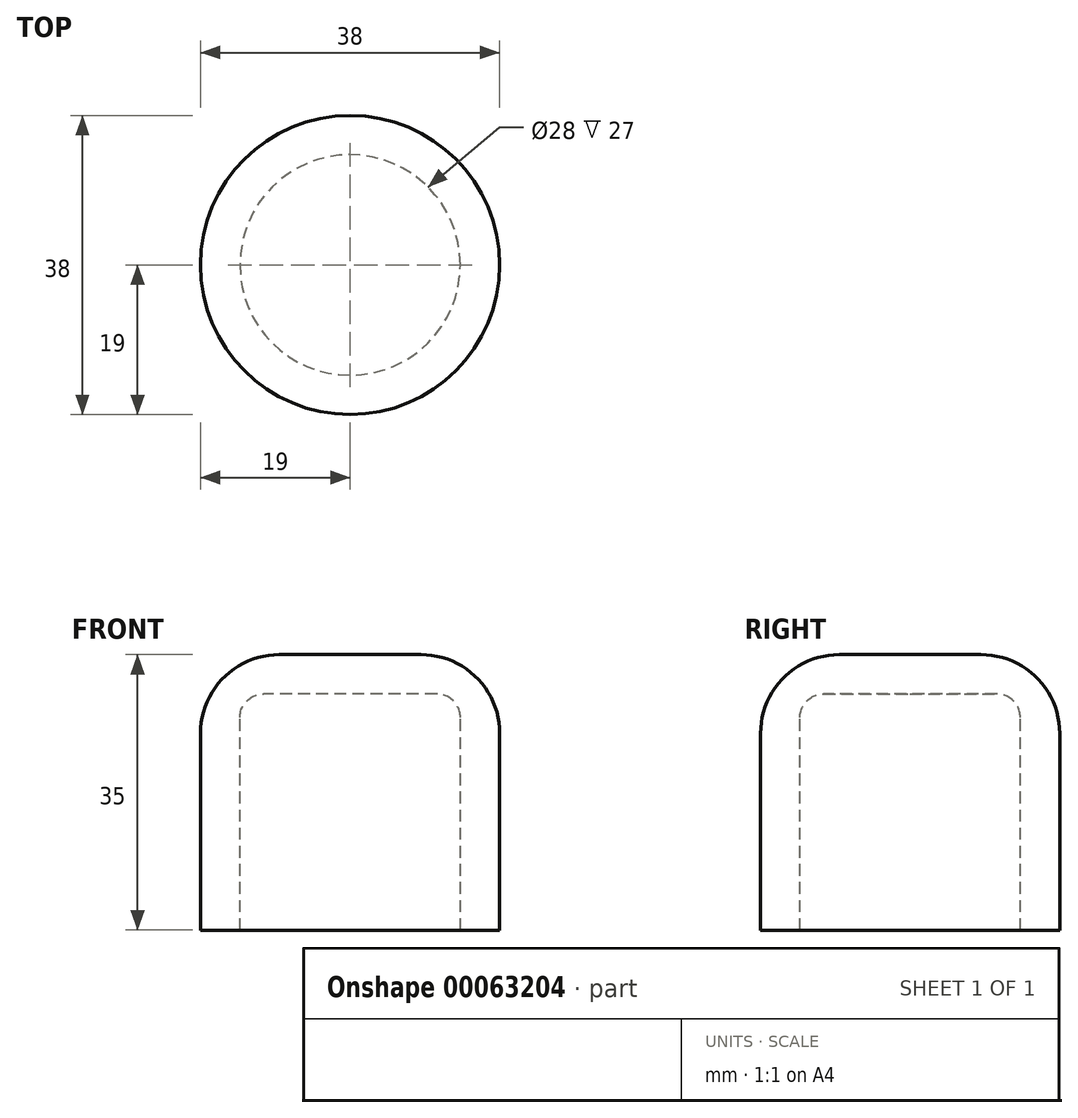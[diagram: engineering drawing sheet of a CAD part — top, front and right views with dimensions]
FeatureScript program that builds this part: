
annotation { "Feature Type Name" : "Feature", "Feature Type Description" : "" }
export const myFeature = defineFeature(function(context is Context, id is Id, definition is map)
    precondition{}
    {
        {
            var Q0;
            Q0=qCreatedBy(makeId("Front.planeOp"),FACE);
            var sketch = newSketch(context, id + "F0", { "sketchPlane" : qUnion([Q0])});
            skLineSegment(sketch, "E0", {"start": v(-14, -1.38) * mm, "end": v(-14, 25.62) * mm});
            skLineSegment(sketch, "E1", {"start": v(-11, 28.62) * mm, "end": v(0, 28.62) * mm});
            skLineSegment(sketch, "E2", {"start": v(0, 28.62) * mm, "end": v(0, -1.46) * mm});
            skLineSegment(sketch, "E3.0", {"start": v(-9, 33.62) * mm, "end": v(0, 33.62) * mm});
            skLineSegment(sketch, "E3.1", {"start": v(-19, -1.38) * mm, "end": v(-19, 23.62) * mm});
            skLineSegment(sketch, "E4", {"start": v(0, 28.62) * mm, "end": v(0, 33.62) * mm});
            skLineSegment(sketch, "E5", {"start": v(-14, -1.38) * mm, "end": v(-19, -1.38) * mm});
            skPoint(sketch, "E6.visualSharp", {"position": v(-14, 28.62) * mm});
            skArc(sketch, "E6.filletArc", {"start": v(-11, 28.62) * mm, "mid": v(-13.12, 27.74) * mm, "end": v(-14, 25.62) * mm});
            skPoint(sketch, "E7.visualSharp", {"position": v(-19, 33.62) * mm});
            skArc(sketch, "E7.filletArc", {"start": v(-9, 33.62) * mm, "mid": v(-16.07, 30.7) * mm, "end": v(-19, 23.62) * mm});
            skSolve(sketch);
        }
        {
            var Q0;
            Q0=makeQuery(id+"F0.imprint","IMPRINT",FACE,{"disambiguationData":[TD([[makeQuery(id+"F0.imprint","IMPRINT",EDGE,{"derivedFrom":sQuery(id+"F0.wireOp",EDGE,"E0")}),1.0]])]});
            var Q1;
            Q1=sQuery(id+"F0.wireOp",EDGE,"E2");
            revolve(context, id + "F1", {"entities" : qUnion([Q0]), "axis" : qUnion([Q1]), "revolveType" : RevolveType.FULL});
        }
    });
